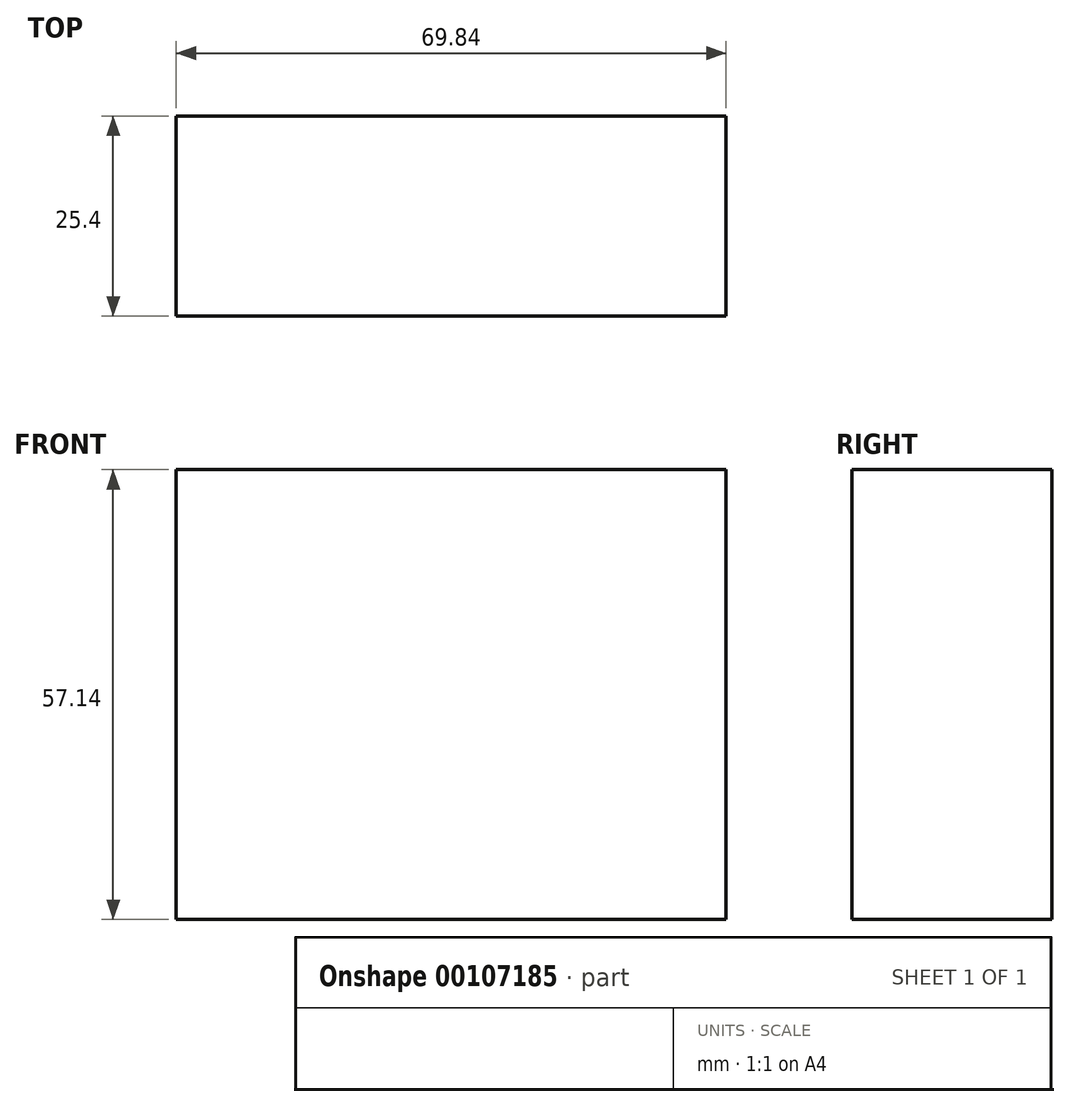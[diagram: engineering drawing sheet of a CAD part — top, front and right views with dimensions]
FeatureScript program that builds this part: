
annotation { "Feature Type Name" : "Feature", "Feature Type Description" : "" }
export const myFeature = defineFeature(function(context is Context, id is Id, definition is map)
    precondition{}
    {
        {
            var Q0;
            Q0=qCreatedBy(makeId("Front.planeOp"),FACE);
            var sketch = newSketch(context, id + "F0", { "sketchPlane" : qUnion([Q0])});
            skLineSegment(sketch, "E0.bottom", {"start": v(-34.92, 28.58) * mm, "end": v(34.93, 28.58) * mm});
            skLineSegment(sketch, "E0.top", {"start": v(-34.93, -28.58) * mm, "end": v(34.92, -28.58) * mm});
            skLineSegment(sketch, "E0.left", {"start": v(-34.92, 28.58) * mm, "end": v(-34.93, -28.58) * mm});
            skLineSegment(sketch, "E0.right", {"start": v(34.93, 28.58) * mm, "end": v(34.92, -28.58) * mm});
            skPoint(sketch, "E0.middle", {"position": v(0, 0) * mm});
            skSolve(sketch);
        }
        {
            var Q0;
            Q0=makeQuery(id+"F0.imprint","IMPRINT",FACE,{"disambiguationData":[TD([[makeQuery(id+"F0.imprint","IMPRINT",EDGE,{"derivedFrom":sQuery(id+"F0.wireOp",EDGE,"E0.bottom")}),-1.0]])]});
            extrude(context, id + "F1", {"entities" : qUnion([Q0]), "depth" : 25.4 * mm});
        }
    });
